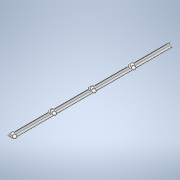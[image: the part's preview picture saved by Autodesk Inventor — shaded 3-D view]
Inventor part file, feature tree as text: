
AUTODESK INVENTOR PART (.ipt)
format: ipt  version: 2020.2 (Build 242310000, 310)  size: 167,936 bytes
history: native  units: in
note: dims shown in document units (in); Inventor stores cm internally (conversion verified against a paired STEP export)
features: sketch x3, hole x2, extrude x1
ambient origin geometry x8: Origin, YZ Plane, XZ Plane, XY Plane, X Axis, Y Axis, Z Axis, Center Point
bodies: Solid1 (feature_tree)
feature tree (6):
  extrude  "Extrusion1"  Depth=1.1811in
  hole  "Hole1"  [1 undecoded]
  hole  "Hole2"  [1 undecoded]
  sketch  "Sketch1"  dims[d0=0.1181in d2=1.1811in]
  sketch  "Sketch2"  dims[d5=0.1181in d6=70.8661in d7=0.0in]
  sketch  "Sketch3"  dims[d8=0.5906in d9=0.5906in d10=0.5906in d11=0.5906in d12=17.7165in d13=17.7165in d14=0.5906in d15=0.5906in d16=17.7165in d17=17.7165in d18=0.5906in d19=0.5906in d20=17.7165in d21=17.7165in d22=0.5906in d23=0.5906in d24=0.15in d25=0.2953in d26=0.1476in d27=0.0984in d28=90.0deg d29=0.3937in d30=0.8108in d31=0.5906in d32=0.5906in d33=17.7165in d34=0.5906in d35=17.7165in d36=17.7165in d37=0.5906in d38=0.5906in d39=0.15in d40=0.2953in d41=0.1476in d42=0.0984in d43=90.0deg d44=0.3937in d45=0.8108in d46=0.0in d47=0.0in d48=0.0in d49=0.0in d50=0.0in d51=0.0in d52=0.0in d53=0.0in d54=0.0in d55=0.0in d56=0.0in d57=0.0in d58=0.0in d59=0.0in d60=0.0in d61=0.0in]
note: 2 required parameter values undecoded (feature->parameter linkage not recoverable at this tier; creation-order binding heuristic only, values carry confidence <= 0.55)
